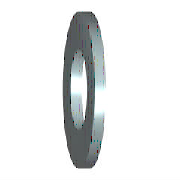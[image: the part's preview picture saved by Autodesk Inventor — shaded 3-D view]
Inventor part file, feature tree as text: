
AUTODESK INVENTOR PART (.ipt)
format: ipt  version: 2020 (Build 240168000, 168)  size: 108,544 bytes
history: native  units: mm (DEFAULTED — no unit token found)
features: other x1, plane x1, sketch x1
ambient origin geometry x7: Origin, YZ Plane, XY Plane, X Axis, Y Axis, Z Axis, Center Point
bodies: Solid1 (feature_tree), Body (feature_tree)
feature tree (3):
  other  "Work Axis1"
  plane  "Work Plane1"
  sketch  "Sketch"  dims[d0=3.2mm d1=7.0mm d2=0.5mm d3=0.0mm d4=0.0mm d5=0.0mm d6=0.0mm d7=0.0mm]
